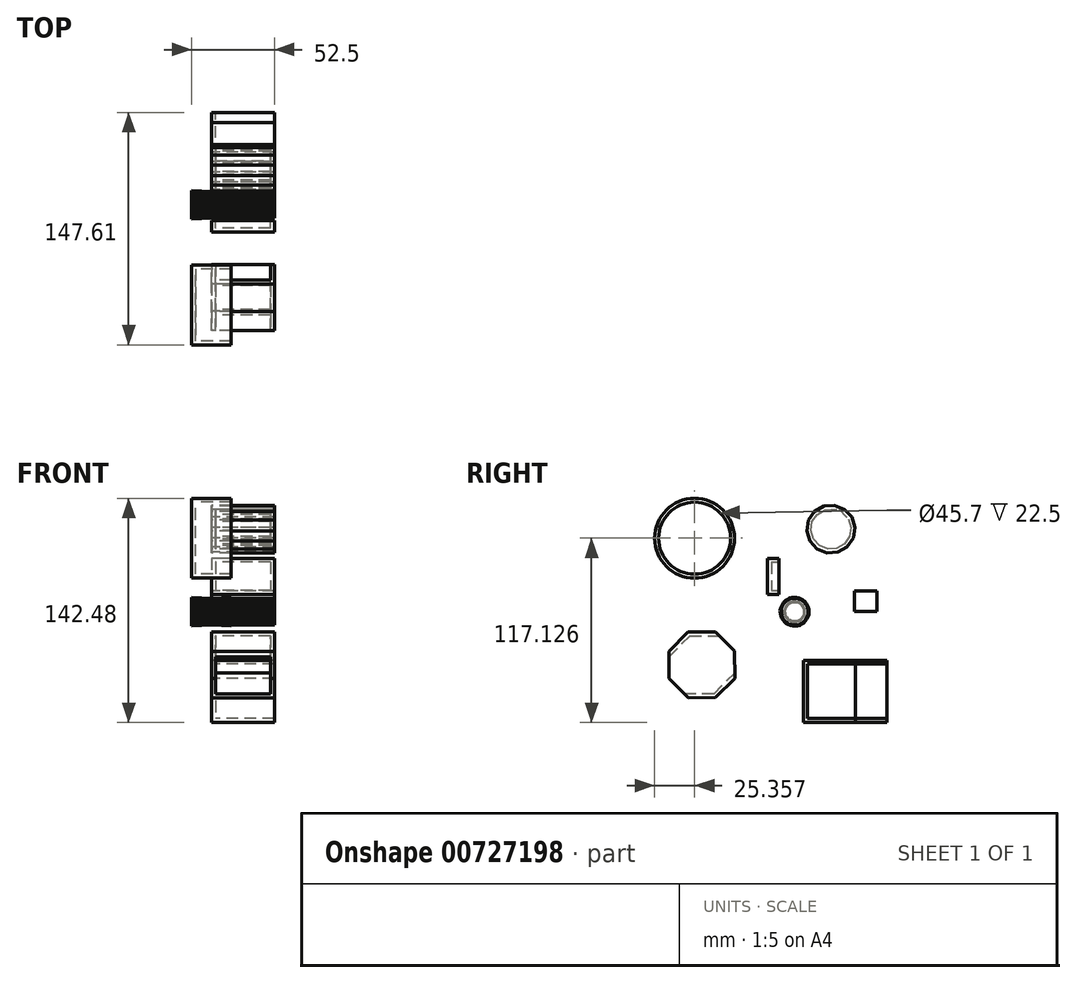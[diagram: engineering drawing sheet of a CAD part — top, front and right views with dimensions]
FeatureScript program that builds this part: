
annotation { "Feature Type Name" : "Feature", "Feature Type Description" : "" }
export const myFeature = defineFeature(function(context is Context, id is Id, definition is map)
    precondition{}
    {
        {
            var Q0;
            Q0=qCreatedBy(makeId("Right.planeOp"),FACE);
            var sketch = newSketch(context, id + "F0", { "sketchPlane" : qUnion([Q0])});
            skCircle(sketch, "E0", {"center": v(-46.4, 55.2) * mm, "radius": 25.35 * mm});
            skCircle(sketch, "E1.cCircle", {"center": v(36.56, 43.17) * mm, "radius": 17.16 * mm, "construction": true});
            skLineSegment(sketch, "E1.0", {"start": v(57.72, 44.68) * mm, "end": v(44.53, 23.52) * mm});
            skLineSegment(sketch, "E1.1", {"start": v(44.53, 23.52) * mm, "end": v(20.33, 29.52) * mm});
            skLineSegment(sketch, "E1.2", {"start": v(20.33, 29.52) * mm, "end": v(18.56, 54.4) * mm});
            skLineSegment(sketch, "E1.3", {"start": v(18.56, 54.4) * mm, "end": v(41.67, 63.76) * mm});
            skLineSegment(sketch, "E1.4", {"start": v(41.67, 63.76) * mm, "end": v(57.72, 44.68) * mm});
            skPoint(sketch, "E1.0.midPoint", {"position": v(51.13, 34.1) * mm});
            skCircle(sketch, "E2.cCircle", {"center": v(-41.75, -18.88) * mm, "radius": 15.48 * mm, "construction": true});
            skLineSegment(sketch, "E2.0", {"start": v(-25.48, -16.3) * mm, "end": v(-27.63, -27.37) * mm});
            skLineSegment(sketch, "E2.1", {"start": v(-27.63, -27.37) * mm, "end": v(-36.39, -34.46) * mm});
            skLineSegment(sketch, "E2.2", {"start": v(-36.39, -34.46) * mm, "end": v(-47.66, -34.26) * mm});
            skLineSegment(sketch, "E2.3", {"start": v(-47.66, -34.26) * mm, "end": v(-56.16, -26.87) * mm});
            skLineSegment(sketch, "E2.4", {"start": v(-56.16, -26.87) * mm, "end": v(-57.92, -15.74) * mm});
            skLineSegment(sketch, "E2.5", {"start": v(-57.92, -15.74) * mm, "end": v(-52.12, -6.08) * mm});
            skLineSegment(sketch, "E2.6", {"start": v(-52.12, -6.08) * mm, "end": v(-41.46, -2.4) * mm});
            skLineSegment(sketch, "E2.7", {"start": v(-41.46, -2.4) * mm, "end": v(-30.94, -6.45) * mm});
            skLineSegment(sketch, "E2.8", {"start": v(-30.94, -6.45) * mm, "end": v(-25.48, -16.3) * mm});
            skPoint(sketch, "E2.0.midPoint", {"position": v(-26.55, -21.84) * mm});
            skLineSegment(sketch, "E3.bottom", {"start": v(0, 14.47) * mm, "end": v(31.7, 14.47) * mm});
            skLineSegment(sketch, "E3.top", {"start": v(0, -8.54) * mm, "end": v(31.7, -8.54) * mm});
            skLineSegment(sketch, "E3.left", {"start": v(0, 14.47) * mm, "end": v(0, -8.54) * mm});
            skLineSegment(sketch, "E3.right", {"start": v(31.7, 14.47) * mm, "end": v(31.7, -8.54) * mm});
            skLineSegment(sketch, "E4.bottom", {"start": v(22.2, -33.87) * mm, "end": v(37.83, -33.87) * mm});
            skLineSegment(sketch, "E4.top", {"start": v(22.2, -68.9) * mm, "end": v(37.83, -68.9) * mm});
            skLineSegment(sketch, "E4.left", {"start": v(22.2, -33.87) * mm, "end": v(22.2, -68.9) * mm});
            skLineSegment(sketch, "E4.right", {"start": v(37.83, -33.87) * mm, "end": v(37.83, -68.9) * mm});
            skLineSegment(sketch, "E5.bottom", {"start": v(53.66, -33.03) * mm, "end": v(64.63, -33.03) * mm});
            skLineSegment(sketch, "E5.top", {"start": v(53.66, -41.68) * mm, "end": v(64.63, -41.68) * mm});
            skLineSegment(sketch, "E5.left", {"start": v(53.66, -33.03) * mm, "end": v(53.66, -41.68) * mm});
            skLineSegment(sketch, "E5.right", {"start": v(64.63, -33.03) * mm, "end": v(64.63, -41.68) * mm});
            skSolve(sketch);
        }
        {
            var Q0;
            Q0=makeQuery(id+"F0.imprint","IMPRINT",FACE,{"disambiguationData":[TD([[makeQuery(id+"F0.imprint","IMPRINT",EDGE,{"derivedFrom":sQuery(id+"F0.wireOp",EDGE,"E0")}),1.0]])]});
            extrude(context, id + "F1", {"entities" : qUnion([Q0]), "endBound" : BoundingType.SYMMETRIC, "depth" : 25 * mm, "offsetDistance" : 25 * mm});
        }
        {
            var Q0;
            Q0=qCreatedBy(makeId("Right.planeOp"),FACE);
            var sketch = newSketch(context, id + "F2", { "sketchPlane" : qUnion([Q0])});
            skCircle(sketch, "E6.cCircle", {"center": v(40.15, 61) * mm, "radius": 14.92 * mm, "construction": true});
            skLineSegment(sketch, "E6.0", {"start": v(50.5, 49.72) * mm, "end": v(44.6, 46.34) * mm});
            skLineSegment(sketch, "E6.1", {"start": v(44.6, 46.34) * mm, "end": v(37.8, 45.87) * mm});
            skLineSegment(sketch, "E6.2", {"start": v(37.8, 45.87) * mm, "end": v(31.47, 48.39) * mm});
            skLineSegment(sketch, "E6.3", {"start": v(31.47, 48.39) * mm, "end": v(26.86, 53.4) * mm});
            skLineSegment(sketch, "E6.4", {"start": v(26.86, 53.4) * mm, "end": v(24.89, 59.92) * mm});
            skLineSegment(sketch, "E6.5", {"start": v(24.89, 59.92) * mm, "end": v(25.93, 66.65) * mm});
            skLineSegment(sketch, "E6.6", {"start": v(25.93, 66.65) * mm, "end": v(29.8, 72.26) * mm});
            skLineSegment(sketch, "E6.7", {"start": v(29.8, 72.26) * mm, "end": v(35.71, 75.64) * mm});
            skLineSegment(sketch, "E6.8", {"start": v(35.71, 75.64) * mm, "end": v(42.5, 76.11) * mm});
            skLineSegment(sketch, "E6.9", {"start": v(42.5, 76.11) * mm, "end": v(48.84, 73.6) * mm});
            skLineSegment(sketch, "E6.10", {"start": v(48.84, 73.6) * mm, "end": v(53.45, 68.58) * mm});
            skLineSegment(sketch, "E6.11", {"start": v(53.45, 68.58) * mm, "end": v(55.42, 62.06) * mm});
            skLineSegment(sketch, "E6.12", {"start": v(55.42, 62.06) * mm, "end": v(54.37, 55.33) * mm});
            skLineSegment(sketch, "E6.13", {"start": v(54.37, 55.33) * mm, "end": v(50.5, 49.72) * mm});
            skPoint(sketch, "E6.0.midPoint", {"position": v(47.55, 48.03) * mm});
            skCircle(sketch, "E7.cCircle", {"center": v(-41.77, -25.25) * mm, "radius": 20.88 * mm, "construction": true});
            skLineSegment(sketch, "E7.0", {"start": v(-20.85, -33.79) * mm, "end": v(-33.02, -46.08) * mm});
            skLineSegment(sketch, "E7.1", {"start": v(-33.02, -46.08) * mm, "end": v(-50.3, -46.17) * mm});
            skLineSegment(sketch, "E7.2", {"start": v(-50.3, -46.17) * mm, "end": v(-62.6, -34) * mm});
            skLineSegment(sketch, "E7.3", {"start": v(-62.6, -34) * mm, "end": v(-62.69, -16.7) * mm});
            skLineSegment(sketch, "E7.4", {"start": v(-62.69, -16.7) * mm, "end": v(-50.52, -4.41) * mm});
            skLineSegment(sketch, "E7.5", {"start": v(-50.52, -4.41) * mm, "end": v(-33.23, -4.33) * mm});
            skLineSegment(sketch, "E7.6", {"start": v(-33.23, -4.33) * mm, "end": v(-20.94, -16.5) * mm});
            skLineSegment(sketch, "E7.7", {"start": v(-20.94, -16.5) * mm, "end": v(-20.85, -33.79) * mm});
            skPoint(sketch, "E7.0.midPoint", {"position": v(-26.93, -39.93) * mm});
            skCircle(sketch, "E8.cCircle", {"center": v(17.17, 8.52) * mm, "radius": 8.51 * mm, "construction": true});
            skLineSegment(sketch, "E8.0", {"start": v(24.48, 4.1) * mm, "end": v(23.65, 2.97) * mm});
            skLineSegment(sketch, "E8.1", {"start": v(23.65, 2.97) * mm, "end": v(22.65, 1.97) * mm});
            skLineSegment(sketch, "E8.2", {"start": v(22.65, 1.97) * mm, "end": v(21.5, 1.16) * mm});
            skLineSegment(sketch, "E8.3", {"start": v(21.5, 1.16) * mm, "end": v(20.23, 0.55) * mm});
            skLineSegment(sketch, "E8.4", {"start": v(20.23, 0.55) * mm, "end": v(18.87, 0.16) * mm});
            skLineSegment(sketch, "E8.5", {"start": v(18.87, 0.16) * mm, "end": v(17.47, -0.01) * mm});
            skLineSegment(sketch, "E8.6", {"start": v(17.47, -0.01) * mm, "end": v(16.06, 0.06) * mm});
            skLineSegment(sketch, "E8.7", {"start": v(16.06, 0.06) * mm, "end": v(14.68, 0.35) * mm});
            skLineSegment(sketch, "E8.8", {"start": v(14.68, 0.35) * mm, "end": v(13.37, 0.87) * mm});
            skLineSegment(sketch, "E8.9", {"start": v(13.37, 0.87) * mm, "end": v(12.16, 1.6) * mm});
            skLineSegment(sketch, "E8.10", {"start": v(12.16, 1.6) * mm, "end": v(11.1, 2.52) * mm});
            skLineSegment(sketch, "E8.11", {"start": v(11.1, 2.52) * mm, "end": v(10.19, 3.6) * mm});
            skLineSegment(sketch, "E8.12", {"start": v(10.19, 3.6) * mm, "end": v(9.47, 4.82) * mm});
            skLineSegment(sketch, "E8.13", {"start": v(9.47, 4.82) * mm, "end": v(8.97, 6.14) * mm});
            skLineSegment(sketch, "E8.14", {"start": v(8.97, 6.14) * mm, "end": v(8.69, 7.52) * mm});
            skLineSegment(sketch, "E8.15", {"start": v(8.69, 7.52) * mm, "end": v(8.64, 8.93) * mm});
            skLineSegment(sketch, "E8.16", {"start": v(8.64, 8.93) * mm, "end": v(8.82, 10.33) * mm});
            skLineSegment(sketch, "E8.17", {"start": v(8.82, 10.33) * mm, "end": v(9.23, 11.68) * mm});
            skLineSegment(sketch, "E8.18", {"start": v(9.23, 11.68) * mm, "end": v(9.86, 12.94) * mm});
            skLineSegment(sketch, "E8.19", {"start": v(9.86, 12.94) * mm, "end": v(10.68, 14.08) * mm});
            skLineSegment(sketch, "E8.20", {"start": v(10.68, 14.08) * mm, "end": v(11.69, 15.08) * mm});
            skLineSegment(sketch, "E8.21", {"start": v(11.69, 15.08) * mm, "end": v(12.84, 15.89) * mm});
            skLineSegment(sketch, "E8.22", {"start": v(12.84, 15.89) * mm, "end": v(14.11, 16.5) * mm});
            skLineSegment(sketch, "E8.23", {"start": v(14.11, 16.5) * mm, "end": v(15.47, 16.9) * mm});
            skLineSegment(sketch, "E8.24", {"start": v(15.47, 16.9) * mm, "end": v(16.87, 17.06) * mm});
            skLineSegment(sketch, "E8.25", {"start": v(16.87, 17.06) * mm, "end": v(18.28, 17) * mm});
            skLineSegment(sketch, "E8.26", {"start": v(18.28, 17) * mm, "end": v(19.66, 16.7) * mm});
            skLineSegment(sketch, "E8.27", {"start": v(19.66, 16.7) * mm, "end": v(20.97, 16.18) * mm});
            skLineSegment(sketch, "E8.28", {"start": v(20.97, 16.18) * mm, "end": v(22.17, 15.45) * mm});
            skLineSegment(sketch, "E8.29", {"start": v(22.17, 15.45) * mm, "end": v(23.24, 14.53) * mm});
            skLineSegment(sketch, "E8.30", {"start": v(23.24, 14.53) * mm, "end": v(24.15, 13.45) * mm});
            skLineSegment(sketch, "E8.31", {"start": v(24.15, 13.45) * mm, "end": v(24.86, 12.23) * mm});
            skLineSegment(sketch, "E8.32", {"start": v(24.86, 12.23) * mm, "end": v(25.37, 10.91) * mm});
            skLineSegment(sketch, "E8.33", {"start": v(25.37, 10.91) * mm, "end": v(25.65, 9.53) * mm});
            skLineSegment(sketch, "E8.34", {"start": v(25.65, 9.53) * mm, "end": v(25.7, 8.12) * mm});
            skLineSegment(sketch, "E8.35", {"start": v(25.7, 8.12) * mm, "end": v(25.52, 6.72) * mm});
            skLineSegment(sketch, "E8.36", {"start": v(25.52, 6.72) * mm, "end": v(25.1, 5.37) * mm});
            skLineSegment(sketch, "E8.37", {"start": v(25.1, 5.37) * mm, "end": v(24.48, 4.1) * mm});
            skPoint(sketch, "E8.0.midPoint", {"position": v(24.07, 3.54) * mm});
            skLineSegment(sketch, "E9.bottom", {"start": v(22.78, -22.31) * mm, "end": v(75.86, -22.31) * mm});
            skLineSegment(sketch, "E9.top", {"start": v(22.78, -61.92) * mm, "end": v(75.86, -61.92) * mm});
            skLineSegment(sketch, "E9.left", {"start": v(22.78, -22.31) * mm, "end": v(22.78, -61.92) * mm});
            skLineSegment(sketch, "E9.right", {"start": v(75.86, -22.31) * mm, "end": v(75.86, -61.92) * mm});
            skLineSegment(sketch, "E10.bottom", {"start": v(0, 42.48) * mm, "end": v(7.31, 42.48) * mm});
            skLineSegment(sketch, "E10.top", {"start": v(0, 19.6) * mm, "end": v(7.31, 19.6) * mm});
            skLineSegment(sketch, "E10.left", {"start": v(0, 42.48) * mm, "end": v(0, 19.6) * mm});
            skLineSegment(sketch, "E10.right", {"start": v(7.31, 42.48) * mm, "end": v(7.31, 19.6) * mm});
            skLineSegment(sketch, "E11.bottom", {"start": v(55.21, 21.8) * mm, "end": v(69.46, 21.8) * mm});
            skLineSegment(sketch, "E11.top", {"start": v(55.21, 8.75) * mm, "end": v(69.46, 8.75) * mm});
            skLineSegment(sketch, "E11.left", {"start": v(55.21, 21.8) * mm, "end": v(55.21, 8.75) * mm});
            skLineSegment(sketch, "E11.right", {"start": v(69.46, 21.8) * mm, "end": v(69.46, 8.75) * mm});
            skSolve(sketch);
        }
        {
            var Q0;
            Q0=makeQuery(id+"F2.imprint","IMPRINT",FACE,{"disambiguationData":[TD([[makeQuery(id+"F2.imprint","IMPRINT",EDGE,{"derivedFrom":sQuery(id+"F2.wireOp",EDGE,"E8.0")}),-1.0]])]});
            extrude(context, id + "F3", {"entities" : qUnion([Q0]), "endBound" : BoundingType.SYMMETRIC, "oppositeDirection" : true, "depth" : 25 * mm, "offsetDistance" : 25 * mm, "hasDraft" : true, "draftAngle" : 3 * degree});
        }
        {
            var Q0;
            Q0=makeQuery(id+"F3.*.split.splitOp","SPLIT",FACE,{"derivedFrom":makeQuery(id+"F3.opExtrude","SWEPT_FACE",FACE,{"disambiguationData":[OSD([sQuery(id+"F2.wireOp",EDGE,"E8.27")])]})});
            var Q1;
            Q1=makeQuery(id+"F3.*.split.splitOp","SPLIT",FACE,{"derivedFrom":makeQuery(id+"F3.opExtrude","SWEPT_FACE",FACE,{"disambiguationData":[OSD([sQuery(id+"F2.wireOp",EDGE,"E8.27")])]}),"isFromBackBody":true});
            var Q2;
            Q2=makeQuery(id+"F3.*.split.splitOp","SPLIT",FACE,{"derivedFrom":makeQuery(id+"F3.opExtrude","SWEPT_FACE",FACE,{"disambiguationData":[OSD([sQuery(id+"F2.wireOp",EDGE,"E8.28")])]}),"isFromBackBody":true});
            var Q3;
            Q3=makeQuery(id+"F3.*.split.splitOp","SPLIT",FACE,{"derivedFrom":makeQuery(id+"F3.opExtrude","SWEPT_FACE",FACE,{"disambiguationData":[OSD([sQuery(id+"F2.wireOp",EDGE,"E8.28")])]})});
            var Q4;
            Q4=makeQuery(id+"F3.opExtrude","CAP_FACE",FACE,{"disambiguationData":[OSD([sQuery(id+"F2.wireOp",EDGE,"E8.0"),sQuery(id+"F2.wireOp",EDGE,"E8.1"),sQuery(id+"F2.wireOp",EDGE,"E8.2"),sQuery(id+"F2.wireOp",EDGE,"E8.3"),sQuery(id+"F2.wireOp",EDGE,"E8.4"),sQuery(id+"F2.wireOp",EDGE,"E8.5"),sQuery(id+"F2.wireOp",EDGE,"E8.6"),sQuery(id+"F2.wireOp",EDGE,"E8.7"),sQuery(id+"F2.wireOp",EDGE,"E8.8"),sQuery(id+"F2.wireOp",EDGE,"E8.9"),sQuery(id+"F2.wireOp",EDGE,"E8.10"),sQuery(id+"F2.wireOp",EDGE,"E8.11"),sQuery(id+"F2.wireOp",EDGE,"E8.12"),sQuery(id+"F2.wireOp",EDGE,"E8.13"),sQuery(id+"F2.wireOp",EDGE,"E8.14"),sQuery(id+"F2.wireOp",EDGE,"E8.15"),sQuery(id+"F2.wireOp",EDGE,"E8.16"),sQuery(id+"F2.wireOp",EDGE,"E8.17"),sQuery(id+"F2.wireOp",EDGE,"E8.18"),sQuery(id+"F2.wireOp",EDGE,"E8.19"),sQuery(id+"F2.wireOp",EDGE,"E8.20"),sQuery(id+"F2.wireOp",EDGE,"E8.21"),sQuery(id+"F2.wireOp",EDGE,"E8.22"),sQuery(id+"F2.wireOp",EDGE,"E8.23"),sQuery(id+"F2.wireOp",EDGE,"E8.24"),sQuery(id+"F2.wireOp",EDGE,"E8.25"),sQuery(id+"F2.wireOp",EDGE,"E8.26"),sQuery(id+"F2.wireOp",EDGE,"E8.27"),sQuery(id+"F2.wireOp",EDGE,"E8.28"),sQuery(id+"F2.wireOp",EDGE,"E8.29"),sQuery(id+"F2.wireOp",EDGE,"E8.30"),sQuery(id+"F2.wireOp",EDGE,"E8.31"),sQuery(id+"F2.wireOp",EDGE,"E8.32"),sQuery(id+"F2.wireOp",EDGE,"E8.33"),sQuery(id+"F2.wireOp",EDGE,"E8.34"),sQuery(id+"F2.wireOp",EDGE,"E8.35"),sQuery(id+"F2.wireOp",EDGE,"E8.36"),sQuery(id+"F2.wireOp",EDGE,"E8.37")])],"isStart":false});
            var Q5;
            Q5=makeQuery(id+"F3.opExtrude","CAP_FACE",FACE,{"disambiguationData":[OSD([sQuery(id+"F2.wireOp",EDGE,"E8.0"),sQuery(id+"F2.wireOp",EDGE,"E8.1"),sQuery(id+"F2.wireOp",EDGE,"E8.2"),sQuery(id+"F2.wireOp",EDGE,"E8.3"),sQuery(id+"F2.wireOp",EDGE,"E8.4"),sQuery(id+"F2.wireOp",EDGE,"E8.5"),sQuery(id+"F2.wireOp",EDGE,"E8.6"),sQuery(id+"F2.wireOp",EDGE,"E8.7"),sQuery(id+"F2.wireOp",EDGE,"E8.8"),sQuery(id+"F2.wireOp",EDGE,"E8.9"),sQuery(id+"F2.wireOp",EDGE,"E8.10"),sQuery(id+"F2.wireOp",EDGE,"E8.11"),sQuery(id+"F2.wireOp",EDGE,"E8.12"),sQuery(id+"F2.wireOp",EDGE,"E8.13"),sQuery(id+"F2.wireOp",EDGE,"E8.14"),sQuery(id+"F2.wireOp",EDGE,"E8.15"),sQuery(id+"F2.wireOp",EDGE,"E8.16"),sQuery(id+"F2.wireOp",EDGE,"E8.17"),sQuery(id+"F2.wireOp",EDGE,"E8.18"),sQuery(id+"F2.wireOp",EDGE,"E8.19"),sQuery(id+"F2.wireOp",EDGE,"E8.20"),sQuery(id+"F2.wireOp",EDGE,"E8.21"),sQuery(id+"F2.wireOp",EDGE,"E8.22"),sQuery(id+"F2.wireOp",EDGE,"E8.23"),sQuery(id+"F2.wireOp",EDGE,"E8.24"),sQuery(id+"F2.wireOp",EDGE,"E8.25"),sQuery(id+"F2.wireOp",EDGE,"E8.26"),sQuery(id+"F2.wireOp",EDGE,"E8.27"),sQuery(id+"F2.wireOp",EDGE,"E8.28"),sQuery(id+"F2.wireOp",EDGE,"E8.29"),sQuery(id+"F2.wireOp",EDGE,"E8.30"),sQuery(id+"F2.wireOp",EDGE,"E8.31"),sQuery(id+"F2.wireOp",EDGE,"E8.32"),sQuery(id+"F2.wireOp",EDGE,"E8.33"),sQuery(id+"F2.wireOp",EDGE,"E8.34"),sQuery(id+"F2.wireOp",EDGE,"E8.35"),sQuery(id+"F2.wireOp",EDGE,"E8.36"),sQuery(id+"F2.wireOp",EDGE,"E8.37")])],"isStart":true});
            shell(context, id + "F4", {"entities" : qUnion([Q0, Q1, Q2, Q3, Q4, Q5]), "thickness" : 2.5 * mm});
        }
        {
            var Q0;
            Q0 = qSketchRegion(id + "F2", true);
            extrude(context, id + "F5", {"entities" : qUnion([Q0]), "operationType" : NewBodyOperationType.ADD, "depth" : 40 * mm, "offsetDistance" : 25 * mm});
        }
        {
            var Q0;
            Q0=makeQuery(id+"F5.opExtrude","SWEPT_FACE",FACE,{"disambiguationData":[OSD([sQuery(id+"F2.wireOp",EDGE,"E10.right")])]});
            shell(context, id + "F6", {"entities" : qUnion([Q0]), "thickness" : 2.5 * mm});
        }
        {
            var Q0;
            Q0=makeQuery(id+"F5.opExtrude","SWEPT_FACE",FACE,{"disambiguationData":[OSD([sQuery(id+"F2.wireOp",EDGE,"E7.3")])]});
            var Q1;
            Q1=makeQuery(id+"F5.opExtrude","SWEPT_FACE",FACE,{"disambiguationData":[OSD([sQuery(id+"F2.wireOp",EDGE,"E7.2")])]});
            var Q2;
            Q2=makeQuery(id+"F5.opExtrude","SWEPT_FACE",FACE,{"disambiguationData":[OSD([sQuery(id+"F2.wireOp",EDGE,"E7.7")])]});
            var Q3;
            Q3=makeQuery(id+"F5.opExtrude","SWEPT_FACE",FACE,{"disambiguationData":[OSD([sQuery(id+"F2.wireOp",EDGE,"E7.6")])]});
            shell(context, id + "F7", {"entities" : qUnion([Q0, Q1, Q2, Q3]), "thickness" : 2.5 * mm});
        }
        {
            var Q0;
            Q0=makeQuery(id+"F5.opExtrude","CAP_FACE",FACE,{"disambiguationData":[OSD([sQuery(id+"F2.wireOp",EDGE,"E8.0"),sQuery(id+"F2.wireOp",EDGE,"E8.1"),sQuery(id+"F2.wireOp",EDGE,"E8.2"),sQuery(id+"F2.wireOp",EDGE,"E8.3"),sQuery(id+"F2.wireOp",EDGE,"E8.4"),sQuery(id+"F2.wireOp",EDGE,"E8.5"),sQuery(id+"F2.wireOp",EDGE,"E8.6"),sQuery(id+"F2.wireOp",EDGE,"E8.7"),sQuery(id+"F2.wireOp",EDGE,"E8.8"),sQuery(id+"F2.wireOp",EDGE,"E8.9"),sQuery(id+"F2.wireOp",EDGE,"E8.10"),sQuery(id+"F2.wireOp",EDGE,"E8.11"),sQuery(id+"F2.wireOp",EDGE,"E8.12"),sQuery(id+"F2.wireOp",EDGE,"E8.13"),sQuery(id+"F2.wireOp",EDGE,"E8.14"),sQuery(id+"F2.wireOp",EDGE,"E8.15"),sQuery(id+"F2.wireOp",EDGE,"E8.16"),sQuery(id+"F2.wireOp",EDGE,"E8.17"),sQuery(id+"F2.wireOp",EDGE,"E8.18"),sQuery(id+"F2.wireOp",EDGE,"E8.19"),sQuery(id+"F2.wireOp",EDGE,"E8.20"),sQuery(id+"F2.wireOp",EDGE,"E8.21"),sQuery(id+"F2.wireOp",EDGE,"E8.22"),sQuery(id+"F2.wireOp",EDGE,"E8.23"),sQuery(id+"F2.wireOp",EDGE,"E8.24"),sQuery(id+"F2.wireOp",EDGE,"E8.25"),sQuery(id+"F2.wireOp",EDGE,"E8.26"),sQuery(id+"F2.wireOp",EDGE,"E8.27"),sQuery(id+"F2.wireOp",EDGE,"E8.28"),sQuery(id+"F2.wireOp",EDGE,"E8.29"),sQuery(id+"F2.wireOp",EDGE,"E8.30"),sQuery(id+"F2.wireOp",EDGE,"E8.31"),sQuery(id+"F2.wireOp",EDGE,"E8.32"),sQuery(id+"F2.wireOp",EDGE,"E8.33"),sQuery(id+"F2.wireOp",EDGE,"E8.34"),sQuery(id+"F2.wireOp",EDGE,"E8.35"),sQuery(id+"F2.wireOp",EDGE,"E8.36"),sQuery(id+"F2.wireOp",EDGE,"E8.37")])],"isStart":true});
            shell(context, id + "F8", {"entities" : qUnion([Q0]), "thickness" : 2.5 * mm});
        }
        {
            var Q0;
            Q0=makeQuery(id+"F5.opExtrude","SWEPT_FACE",FACE,{"disambiguationData":[OSD([sQuery(id+"F2.wireOp",EDGE,"E9.right")])]});
            extrude(context, id + "F9", {"entities" : qUnion([Q0]), "oppositeDirection" : true, "depth" : 20 * mm, "offsetDistance" : 25 * mm});
        }
        {
            var Q0;
            Q0=makeQuery(id+"F5.opExtrude","CAP_FACE",FACE,{"disambiguationData":[OSD([sQuery(id+"F2.wireOp",EDGE,"E9.bottom"),sQuery(id+"F2.wireOp",EDGE,"E9.top"),sQuery(id+"F2.wireOp",EDGE,"E9.left"),sQuery(id+"F2.wireOp",EDGE,"E9.right")])],"isStart":false});
            var Q1;
            Q1=makeQuery(id+"F5.opExtrude","SWEPT_FACE",FACE,{"disambiguationData":[OSD([sQuery(id+"F2.wireOp",EDGE,"E9.right")])]});
            var Q2;
            Q2=makeQuery(id+"F5.opExtrude","SWEPT_FACE",FACE,{"disambiguationData":[OSD([sQuery(id+"F2.wireOp",EDGE,"E6.9")])]});
            shell(context, id + "F10", {"entities" : qUnion([Q0, Q1, Q2]), "thickness" : 2.5 * mm});
        }
        {
            var Q0;
            Q0=makeQuery(id+"F1.opExtrude","CAP_FACE",FACE,{"disambiguationData":[OSD([sQuery(id+"F0.wireOp",EDGE,"E0")])],"isStart":false});
            shell(context, id + "F11", {"entities" : qUnion([Q0]), "thickness" : 2.5 * mm});
        }
    });
